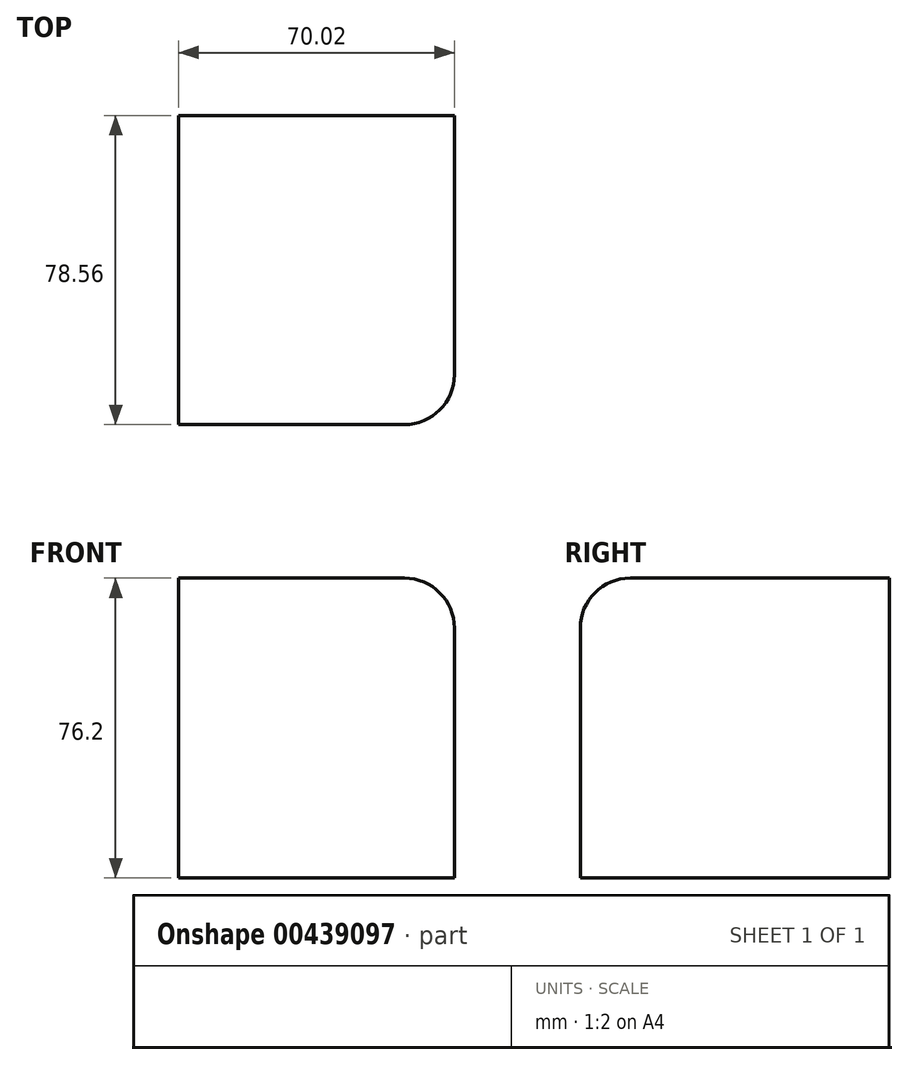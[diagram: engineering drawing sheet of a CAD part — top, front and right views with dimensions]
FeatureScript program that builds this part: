
annotation { "Feature Type Name" : "Feature", "Feature Type Description" : "" }
export const myFeature = defineFeature(function(context is Context, id is Id, definition is map)
    precondition{}
    {
        {
            var Q0;
            Q0=qCreatedBy(makeId("Top.planeOp"),FACE);
            var sketch = newSketch(context, id + "F0", { "sketchPlane" : qUnion([Q0])});
            skLineSegment(sketch, "E0.bottom", {"start": v(-30.52, 37.16) * mm, "end": v(39.5, 37.16) * mm});
            skLineSegment(sketch, "E0.top", {"start": v(-30.52, -41.4) * mm, "end": v(39.5, -41.4) * mm});
            skLineSegment(sketch, "E0.left", {"start": v(-30.52, 37.16) * mm, "end": v(-30.52, -41.4) * mm});
            skLineSegment(sketch, "E0.right", {"start": v(39.5, 37.16) * mm, "end": v(39.5, -41.4) * mm});
            skSolve(sketch);
        }
        {
            var Q0;
            Q0=makeQuery(id+"F0.imprint","IMPRINT",FACE,{"disambiguationData":[TD([[makeQuery(id+"F0.imprint","IMPRINT",EDGE,{"derivedFrom":sQuery(id+"F0.wireOp",EDGE,"E0.bottom")}),-1.0]])]});
            extrude(context, id + "F1", {"entities" : qUnion([Q0]), "depth" : 76.2 * mm});
        }
        {
            var Q0;
            Q0=makeQuery(id+"F1.opExtrude","CAP_EDGE",EDGE,{"disambiguationData":[OSD([sQuery(id+"F0.wireOp",EDGE,"E0.top")])],"isStart":false});
            fillet(context, id + "F2", {"entities" : qUnion([Q0]), "radius" : 12.7 * mm, "tangentPropagation" : true, "allowEdgeOverflow" : false});
        }
        {
            var Q0;
            Q0=makeQuery(id+"F1.opExtrude","CAP_EDGE",EDGE,{"disambiguationData":[OSD([sQuery(id+"F0.wireOp",EDGE,"E0.right")])],"isStart":false});
            fillet(context, id + "F3", {"entities" : qUnion([Q0]), "radius" : 12.7 * mm, "tangentPropagation" : true, "allowEdgeOverflow" : false});
        }
    });
